# Revit family: Control_Panels-Lutron-Panel_Enclosure-LV21 NEW
name_source: partatom
category: Electrical Equipment
revit_build: Autodesk Revit 2017 (Build: 20160720_1515(x64)
units: mm (PartAtom-declared; Revit-internal decimal feet)

## family parameters
Cut with Voids When Loaded = No
Host = Face
OmniClass Number = 23.80.30.11.17
OmniClass Title = Distribution Boards and Control Panels
Panel Configuration = Two Columns, Circuits Across
Part Type = Panelboard
Room Calculation Point = No
Round Connector Dimension = Use Radius
Shared = No

## types (2) — shared parameters
Assembly Code = D5020
Default Elevation = 0"
Description = Low-Voltage Enclosure
Electrical Potential = 1 V
Feed Through Control Circuit Voltage = 1 V
Finish = Steel - Lutron - Black
Frequency = 60 Hz
Ground Bus = Yes
Instruction Sheet Link = http://www.lutron.com
Load Classification = Power
MCB Rating = 1 A
Manufacturer = Lutron Electronics Co., Inc
Manufacturer Fax Number = 610-282-1243
Neutral Bus = Yes
Neutral Rating = 0.00%
Number of Poles = 1
Offset C = 4 3/32"
Overall Depth = 4 3/32"
Overall Height = 21"
Overall Width = 14 3/8"
Performance URL = http://www.lutron.com
Phase = 1
Power Factor = 1
Product Documentation Link = http://www.lutron.com
Product Name = Low-Voltage Enclosure
Product Page URL = http://www.lutron.com
Recessed = No
Series = HomeWorks QS
SubFeed Lugs = No
Surface = Yes
URL = http://www.lutron.com
Unit Weight = 0.00 lb
Version = 2017 - v1.0a
Video Link = https://www.youtube.com
Warranty URL = http://www.lutron.com
zero-valued in all types: Cost

## per-type parameters (varying)
| type | Voltage |
| HQ-LV21-120 | 120.00 V |
| L-LV21-230 | 230.00 V |

note: column(s) folded — value = type name in every type: Model

## geometry (parser evidence)
native form markers: Sweep x2
no freeform markers — native parametric forms only
